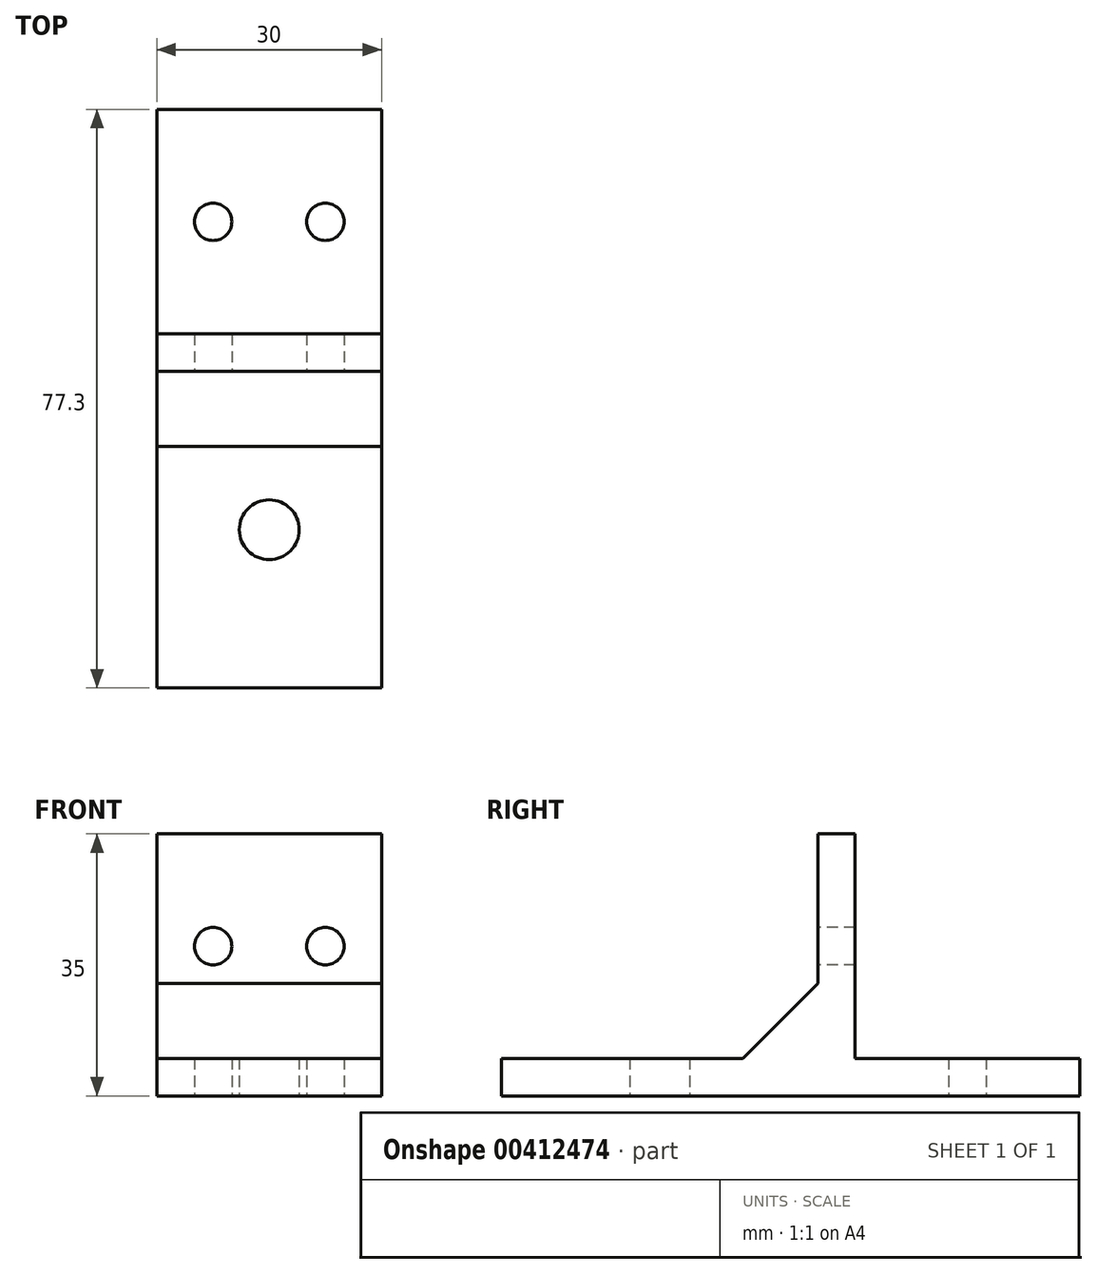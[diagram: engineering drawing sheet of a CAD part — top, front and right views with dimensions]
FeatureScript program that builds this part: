
annotation { "Feature Type Name" : "Feature", "Feature Type Description" : "" }
export const myFeature = defineFeature(function(context is Context, id is Id, definition is map)
    precondition{}
    {
        {
            var Q0;
            Q0=qCreatedBy(makeId("Top.planeOp"),FACE);
            var sketch = newSketch(context, id + "F0", { "sketchPlane" : qUnion([Q0])});
            skLineSegment(sketch, "E0.bottom", {"start": v(15, 38.65) * mm, "end": v(-15, 38.65) * mm});
            skLineSegment(sketch, "E0.top", {"start": v(15, -38.65) * mm, "end": v(-15, -38.65) * mm});
            skLineSegment(sketch, "E0.left", {"start": v(15, 38.65) * mm, "end": v(15, -38.65) * mm});
            skLineSegment(sketch, "E0.right", {"start": v(-15, 38.65) * mm, "end": v(-15, -38.65) * mm});
            skPoint(sketch, "E0.middle", {"position": v(0, 0) * mm});
            skLineSegment(sketch, "E1", {"start": v(-15, 8.65) * mm, "end": v(15, 8.65) * mm});
            skLineSegment(sketch, "E2.0", {"start": v(-15, 3.65) * mm, "end": v(15, 3.65) * mm});
            skPoint(sketch, "E3", {"position": v(0, -17.5) * mm});
            skCircle(sketch, "E4", {"center": v(0, -17.5) * mm, "radius": 4 * mm});
            skCircle(sketch, "E5", {"center": v(-7.5, 23.65) * mm, "radius": 2.5 * mm});
            skCircle(sketch, "E6", {"center": v(7.5, 23.65) * mm, "radius": 2.5 * mm});
            skSolve(sketch);
        }
        {
            var Q0;
            {var subQ0=sQuery(id+"F0.wireOp",EDGE,"E0.bottom");Q0=makeQuery(id+"F0.imprint","IMPRINT",FACE,{"disambiguationData":[TD([[makeQuery(id+"F0.imprint","IMPRINT",EDGE,{"derivedFrom":subQ0}),1.0]])]});}
            var Q1;
            {var subQ0=sQuery(id+"F0.wireOp",EDGE,"E1");Q1=makeQuery(id+"F0.imprint","IMPRINT",FACE,{"disambiguationData":[TD([[makeQuery(id+"F0.imprint","IMPRINT",EDGE,{"derivedFrom":subQ0}),-1.0]])]});}
            var Q2;
            {var subQ1=sQuery(id+"F0.wireOp",EDGE,"E0.top");Q2=makeQuery(id+"F0.imprint","IMPRINT",FACE,{"disambiguationData":[TD([[makeQuery(id+"F0.imprint","IMPRINT",EDGE,{"derivedFrom":subQ1}),-1.0]])]});}
            extrude(context, id + "F1", {"entities" : qUnion([Q0, Q1, Q2]), "depth" : 5 * mm});
        }
        {
            var Q0;
            {var subQ0=sQuery(id+"F0.wireOp",EDGE,"E1");Q0=makeQuery(id+"F0.imprint","IMPRINT",FACE,{"disambiguationData":[TD([[makeQuery(id+"F0.imprint","IMPRINT",EDGE,{"derivedFrom":subQ0}),-1.0]])]});}
            extrude(context, id + "F2", {"entities" : qUnion([Q0]), "operationType" : NewBodyOperationType.ADD, "depth" : 35 * mm});
        }
        {
            var Q0;
            Q0=qCreatedBy(makeId("Front.planeOp"),FACE);
            var sketch = newSketch(context, id + "F3", { "sketchPlane" : qUnion([Q0])});
            skLineSegment(sketch, "E7.bottom", {"start": v(0, 0) * mm, "end": v(-15, 0) * mm});
            skLineSegment(sketch, "E7.top", {"start": v(0, 35) * mm, "end": v(-15, 35) * mm});
            skLineSegment(sketch, "E7.left", {"start": v(0, 0) * mm, "end": v(0, 35) * mm});
            skLineSegment(sketch, "E7.right", {"start": v(-15, 0) * mm, "end": v(-15, 35) * mm});
            skLineSegment(sketch, "E8.MirrorCS", {"start": v(0, 35) * mm, "end": v(15, 35) * mm});
            skLineSegment(sketch, "E9.MirrorCS", {"start": v(15, 0) * mm, "end": v(15, 35) * mm});
            skLineSegment(sketch, "E10.MirrorCS", {"start": v(0, 0) * mm, "end": v(15, 0) * mm});
            skPoint(sketch, "E11", {"position": v(-7.5, 20) * mm});
            skPoint(sketch, "E12.MirrorP", {"position": v(7.5, 20) * mm});
            skSolve(sketch);
        }
        {
            var Q0;
            Q0=sQuery(id+"F3.wireOp",VERTEX,"E11");
            var Q1;
            Q1=sQuery(id+"F3.wireOp",VERTEX,"E12.MirrorP");
            var Q2;
            Q2=makeQuery(id+"F1.opExtrude","SWEPT_BODY",BODY,{"disambiguationData":[OSD([sQuery(id+"F0.wireOp",EDGE,"E0.bottom"),sQuery(id+"F0.wireOp",EDGE,"E0.top"),sQuery(id+"F0.wireOp",EDGE,"E0.left"),sQuery(id+"F0.wireOp",EDGE,"E0.right"),sQuery(id+"F0.wireOp",EDGE,"E4"),sQuery(id+"F0.wireOp",EDGE,"E5"),sQuery(id+"F0.wireOp",EDGE,"E6")])]});
            hole(context, id + "F4", {"style" : HoleStyle.SIMPLE, "endStyle" : HoleEndStyle.BLIND, "holeDiameter" : 5 * mm, "holeDepth" : 12.7 * mm, "isTappedThrough" : true, "tappedDepth" : 12 * mm, "tapClearance" : 3, "locations" : qUnion([Q0, Q1]), "scope" : qUnion([Q2])});
        }
        {
            var Q0;
            Q0=makeQuery(id+"F2.boolean.opBoolean","INTERSECT",EDGE,{"derivedFrom":[makeQuery(id+"F1.opExtrude","CAP_FACE",FACE,{"disambiguationData":[OSD([sQuery(id+"F0.wireOp",EDGE,"E0.bottom"),sQuery(id+"F0.wireOp",EDGE,"E0.top"),sQuery(id+"F0.wireOp",EDGE,"E0.left"),sQuery(id+"F0.wireOp",EDGE,"E0.right"),sQuery(id+"F0.wireOp",EDGE,"E4"),sQuery(id+"F0.wireOp",EDGE,"E5"),sQuery(id+"F0.wireOp",EDGE,"E6")])],"isStart":false}),makeQuery(id+"F2.opExtrude","SWEPT_FACE",FACE,{"disambiguationData":[OSD([sQuery(id+"F0.wireOp",EDGE,"E2.0")])]})]});
            chamfer(context, id + "F5", {"entities" : qUnion([Q0]), "width" : 10 * mm, "tangentPropagation" : true});
        }
    });
